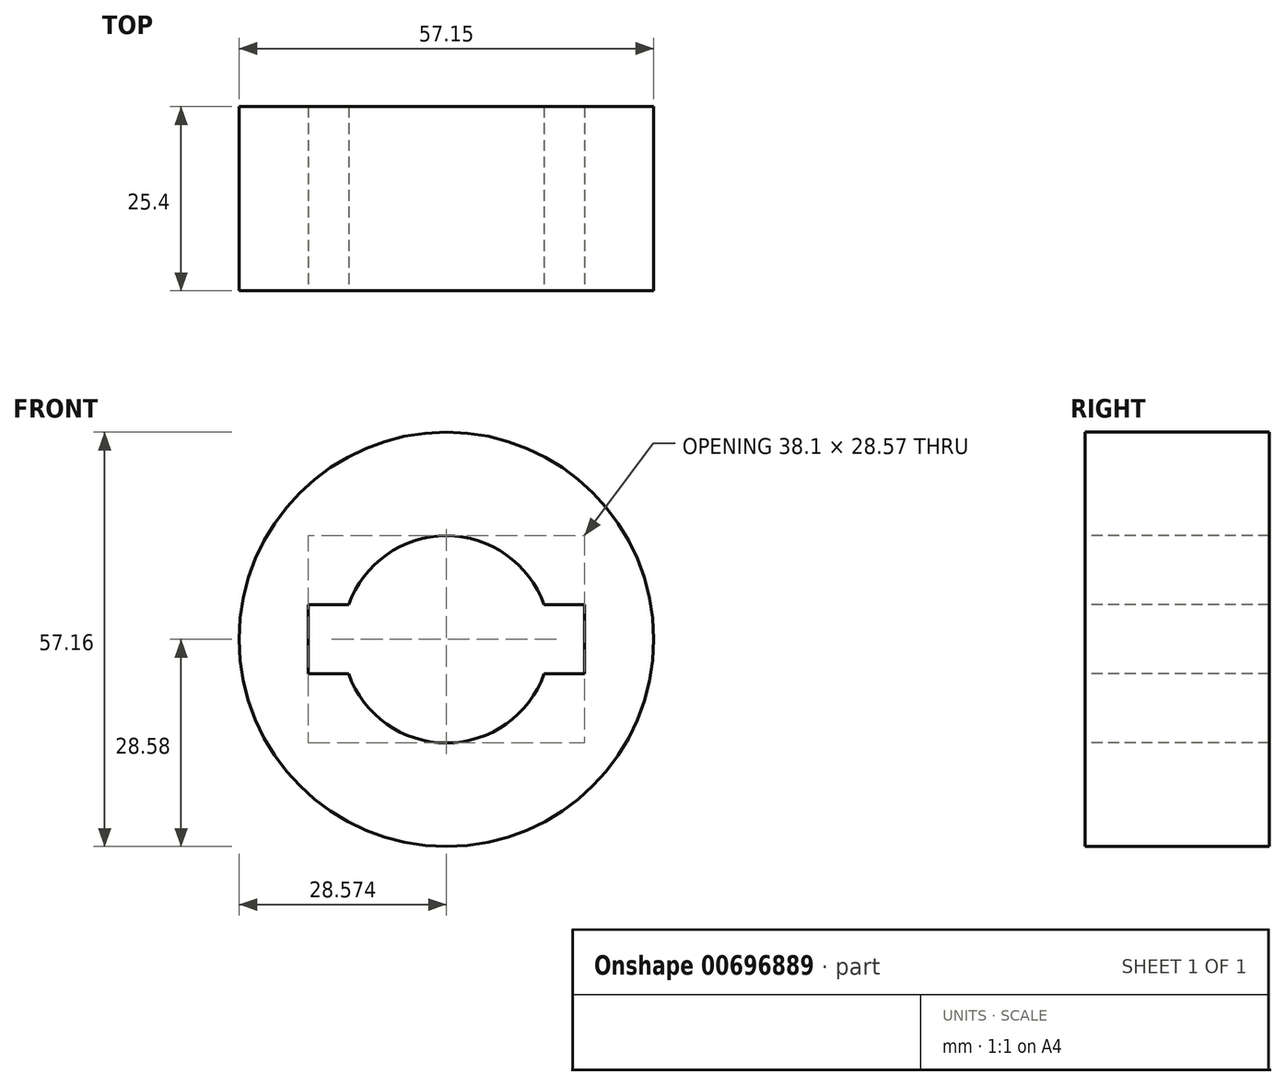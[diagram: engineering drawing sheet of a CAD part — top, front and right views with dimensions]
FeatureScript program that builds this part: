
annotation { "Feature Type Name" : "Feature", "Feature Type Description" : "" }
export const myFeature = defineFeature(function(context is Context, id is Id, definition is map)
    precondition{}
    {
        {
            var Q0;
            Q0=qCreatedBy(makeId("Front.planeOp"),FACE);
            var sketch = newSketch(context, id + "F0", { "sketchPlane" : qUnion([Q0])});
            skCircle(sketch, "E0", {"center": v(-30.26, 0) * mm, "radius": 28.58 * mm});
            skCircle(sketch, "E1", {"center": v(23.72, 0) * mm, "radius": 19.05 * mm});
            skLineSegment(sketch, "E2", {"start": v(-25.21, 28.13) * mm, "end": v(27.08, 18.75) * mm});
            skLineSegment(sketch, "E3", {"start": v(-25.21, -28.13) * mm, "end": v(27.08, -18.75) * mm});
            skCircle(sketch, "E4", {"center": v(-30.26, 0) * mm, "radius": 14.29 * mm});
            skCircle(sketch, "E5", {"center": v(23.72, 0) * mm, "radius": 14.29 * mm});
            skLineSegment(sketch, "E6.bottom", {"start": v(-11.2, -4.76) * mm, "end": v(-49.3, -4.76) * mm});
            skLineSegment(sketch, "E6.top", {"start": v(-11.2, 4.76) * mm, "end": v(-49.3, 4.76) * mm});
            skLineSegment(sketch, "E6.left", {"start": v(-11.2, -4.76) * mm, "end": v(-11.2, 4.76) * mm});
            skLineSegment(sketch, "E6.right", {"start": v(-49.3, -4.76) * mm, "end": v(-49.3, 4.76) * mm});
            skSolve(sketch);
        }
        {
            var Q0;
            {var subQ7=sQuery(id+"F0.wireOp",EDGE,"E6.left");Q0=makeQuery(id+"F0.imprint","IMPRINT",FACE,{"disambiguationData":[TD([[makeQuery(id+"F0.imprint","IMPRINT",EDGE,{"derivedFrom":subQ7}),-1.0]])]});}
            extrude(context, id + "F1", {"entities" : qUnion([Q0]), "oppositeDirection" : true, "depth" : 25.4 * mm, "offsetDistance" : 25.4 * mm});
        }
    });
